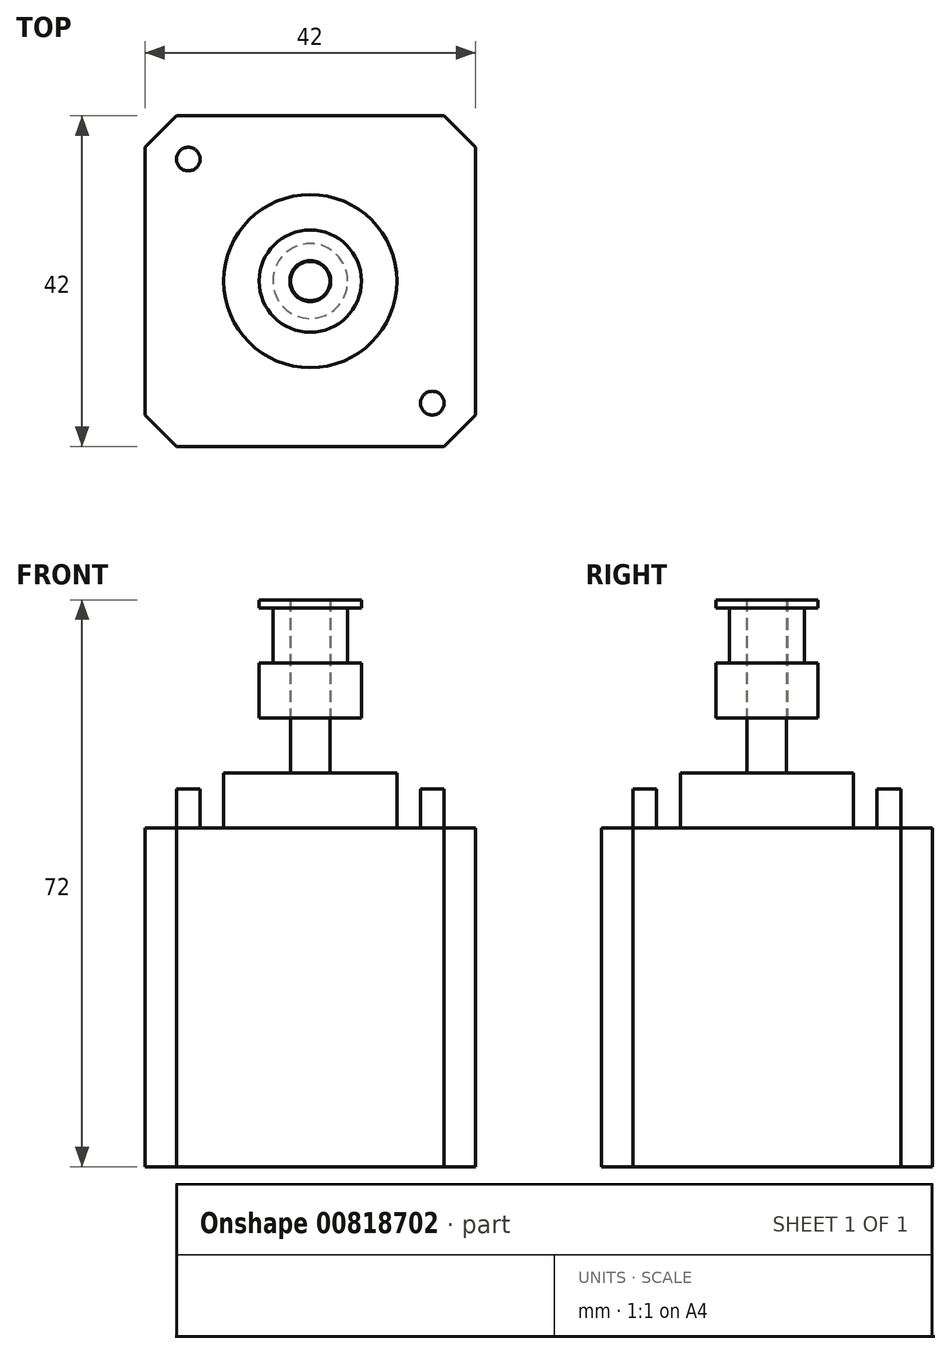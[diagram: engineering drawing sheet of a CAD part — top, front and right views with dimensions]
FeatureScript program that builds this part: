
annotation { "Feature Type Name" : "Feature", "Feature Type Description" : "" }
export const myFeature = defineFeature(function(context is Context, id is Id, definition is map)
    precondition{}
    {
        {
            var Q0;
            Q0=qCreatedBy(makeId("Top.planeOp"),FACE);
            var sketch = newSketch(context, id + "F0", { "sketchPlane" : qUnion([Q0])});
            skLineSegment(sketch, "E0.bottom", {"start": v(21, 21) * mm, "end": v(-21, 21) * mm});
            skLineSegment(sketch, "E0.top", {"start": v(21, -21) * mm, "end": v(-21, -21) * mm});
            skLineSegment(sketch, "E0.left", {"start": v(21, 21) * mm, "end": v(21, -21) * mm});
            skLineSegment(sketch, "E0.right", {"start": v(-21, 21) * mm, "end": v(-21, -21) * mm});
            skPoint(sketch, "E0.middle", {"position": v(0, 0) * mm});
            skSolve(sketch);
        }
        {
            var Q0;
            Q0=makeQuery(id+"F0.imprint","IMPRINT",FACE,{"disambiguationData":[TD([[makeQuery(id+"F0.imprint","IMPRINT",EDGE,{"derivedFrom":sQuery(id+"F0.wireOp",EDGE,"E0.bottom")}),1.0]])]});
            extrude(context, id + "F1", {"entities" : qUnion([Q0]), "depth" : 48 * mm, "offsetDistance" : 25 * mm});
        }
        {
            var Q0;
            Q0=makeQuery(id+"F1.opExtrude","SWEPT_EDGE",EDGE,{"disambiguationData":[OSD([sQuery(id+"F0.wireOp",EDGE,"E0.top"),sQuery(id+"F0.wireOp",EDGE,"E0.right")])]});
            var Q1;
            Q1=makeQuery(id+"F1.opExtrude","SWEPT_EDGE",EDGE,{"disambiguationData":[OSD([sQuery(id+"F0.wireOp",EDGE,"E0.top"),sQuery(id+"F0.wireOp",EDGE,"E0.left")])]});
            var Q2;
            Q2=makeQuery(id+"F1.opExtrude","SWEPT_EDGE",EDGE,{"disambiguationData":[OSD([sQuery(id+"F0.wireOp",EDGE,"E0.bottom"),sQuery(id+"F0.wireOp",EDGE,"E0.left")])]});
            var Q3;
            Q3=makeQuery(id+"F1.opExtrude","SWEPT_EDGE",EDGE,{"disambiguationData":[OSD([sQuery(id+"F0.wireOp",EDGE,"E0.bottom"),sQuery(id+"F0.wireOp",EDGE,"E0.right")])]});
            chamfer(context, id + "F2", {"entities" : qUnion([Q0, Q1, Q2, Q3]), "width" : 4 * mm, "tangentPropagation" : true});
        }
        {
            var Q0;
            Q0=makeQuery(id+"F1.opExtrude","CAP_FACE",FACE,{"disambiguationData":[OSD([sQuery(id+"F0.wireOp",EDGE,"E0.bottom"),sQuery(id+"F0.wireOp",EDGE,"E0.top"),sQuery(id+"F0.wireOp",EDGE,"E0.left"),sQuery(id+"F0.wireOp",EDGE,"E0.right")])],"isStart":false});
            var sketch = newSketch(context, id + "F3", { "sketchPlane" : qUnion([Q0])});
            skCircle(sketch, "E1", {"center": v(0, 0) * mm, "radius": 11 * mm});
            skCircle(sketch, "E2", {"center": v(0, 0) * mm, "radius": 2.5 * mm});
            skPoint(sketch, "E3", {"position": v(-15.5, -15.5) * mm});
            skCircle(sketch, "E4", {"center": v(-15.5, -15.5) * mm, "radius": 1.5 * mm});
            skCircle(sketch, "E5.MirrorC", {"center": v(15.5, -15.5) * mm, "radius": 1.5 * mm});
            skCircle(sketch, "E6.MirrorC", {"center": v(15.5, 15.5) * mm, "radius": 1.5 * mm});
            skCircle(sketch, "E7.MirrorC", {"center": v(-15.5, 15.5) * mm, "radius": 1.5 * mm});
            skSolve(sketch);
        }
        {
            var Q0;
            Q0=makeQuery(id+"F3.imprint","IMPRINT",FACE,{"disambiguationData":[TD([[makeQuery(id+"F3.imprint","IMPRINT",EDGE,{"derivedFrom":sQuery(id+"F3.wireOp",EDGE,"E2")}),1.0]])]});
            extrude(context, id + "F4", {"entities" : qUnion([Q0]), "operationType" : NewBodyOperationType.ADD, "depth" : 24 * mm, "offsetDistance" : 25 * mm});
        }
        {
            var Q0;
            Q0=makeQuery(id+"F3.imprint","IMPRINT",FACE,{"disambiguationData":[TD([[makeQuery(id+"F3.imprint","IMPRINT",EDGE,{"derivedFrom":sQuery(id+"F3.wireOp",EDGE,"E1")}),1.0]])]});
            var Q1;
            Q1=makeQuery(id+"F3.imprint","IMPRINT",FACE,{"disambiguationData":[TD([[makeQuery(id+"F3.imprint","IMPRINT",EDGE,{"derivedFrom":sQuery(id+"F3.wireOp",EDGE,"E2")}),1.0]])]});
            extrude(context, id + "F5", {"entities" : qUnion([Q0, Q1]), "operationType" : NewBodyOperationType.ADD, "depth" : 2 * mm, "offsetDistance" : 25 * mm});
        }
        {
            var Q0;
            Q0=makeQuery(id+"F3.imprint","IMPRINT",FACE,{"disambiguationData":[TD([[makeQuery(id+"F3.imprint","IMPRINT",EDGE,{"derivedFrom":sQuery(id+"F3.wireOp",EDGE,"E5.MirrorC")}),-1.0]])]});
            var Q1;
            Q1=makeQuery(id+"F3.imprint","IMPRINT",FACE,{"disambiguationData":[TD([[makeQuery(id+"F3.imprint","IMPRINT",EDGE,{"derivedFrom":sQuery(id+"F3.wireOp",EDGE,"E6.MirrorC")}),1.0]])]});
            var Q2;
            Q2=makeQuery(id+"F3.imprint","IMPRINT",FACE,{"disambiguationData":[TD([[makeQuery(id+"F3.imprint","IMPRINT",EDGE,{"derivedFrom":sQuery(id+"F3.wireOp",EDGE,"E7.MirrorC")}),-1.0]])]});
            var Q3;
            Q3=makeQuery(id+"F3.imprint","IMPRINT",FACE,{"disambiguationData":[TD([[makeQuery(id+"F3.imprint","IMPRINT",EDGE,{"derivedFrom":sQuery(id+"F3.wireOp",EDGE,"E4")}),1.0]])]});
            extrude(context, id + "F6", {"entities" : qUnion([Q0, Q1, Q2, Q3]), "operationType" : NewBodyOperationType.REMOVE, "oppositeDirection" : true, "depth" : 5 * mm, "offsetDistance" : 25 * mm});
        }
        {
            var Q0;
            Q0=qCreatedBy(makeId("Front.planeOp"),FACE);
            var sketch = newSketch(context, id + "F7", { "sketchPlane" : qUnion([Q0])});
            skLineSegment(sketch, "E8", {"start": v(0, 57) * mm, "end": v(6.5, 57) * mm, "construction": true});
            skLineSegment(sketch, "E9", {"start": v(6.5, 57) * mm, "end": v(6.5, 64) * mm});
            skLineSegment(sketch, "E10", {"start": v(6.5, 64) * mm, "end": v(4.75, 64) * mm});
            skLineSegment(sketch, "E11", {"start": v(4.75, 64) * mm, "end": v(4.75, 71) * mm});
            skLineSegment(sketch, "E12", {"start": v(4.75, 71) * mm, "end": v(6.5, 71) * mm});
            skLineSegment(sketch, "E13", {"start": v(6.5, 71) * mm, "end": v(6.5, 72) * mm});
            skLineSegment(sketch, "E14", {"start": v(6.5, 72) * mm, "end": v(0, 72) * mm, "construction": true});
            skLineSegment(sketch, "E15", {"start": v(0, 72) * mm, "end": v(0, 57) * mm});
            skLineSegment(sketch, "E16", {"start": v(0, 72) * mm, "end": v(0, 82) * mm, "construction": true});
            skLineSegment(sketch, "E17", {"start": v(6.5, 57) * mm, "end": v(2.6, 57) * mm});
            skLineSegment(sketch, "E18", {"start": v(2.6, 57) * mm, "end": v(2.6, 72) * mm});
            skLineSegment(sketch, "E19", {"start": v(2.6, 72) * mm, "end": v(6.5, 72) * mm});
            skLineSegment(sketch, "E20.0", {"start": v(-2.5, 72) * mm, "end": v(2.5, 72) * mm});
            skSolve(sketch);
        }
        {
            var Q0;
            Q0=makeQuery(id+"F7.imprint","IMPRINT",FACE,{"disambiguationData":[TD([[makeQuery(id+"F7.imprint","IMPRINT",EDGE,{"derivedFrom":sQuery(id+"F7.wireOp",EDGE,"E8")}),1.0]])]});
            var Q1;
            Q1=makeQuery(id+"F7.imprint","IMPRINT",FACE,{"disambiguationData":[TD([[makeQuery(id+"F7.imprint","IMPRINT",EDGE,{"derivedFrom":sQuery(id+"F7.wireOp",EDGE,"E9")}),1.0]])]});
            var Q2;
            Q2=sQuery(id+"F7.wireOp",EDGE,"E16");
            revolve(context, id + "F8", {"surfaceOperationType" : NewSurfaceOperationType.NEW, "entities" : qUnion([Q0, Q1]), "axis" : qUnion([Q2]), "revolveType" : RevolveType.FULL});
        }
    });
